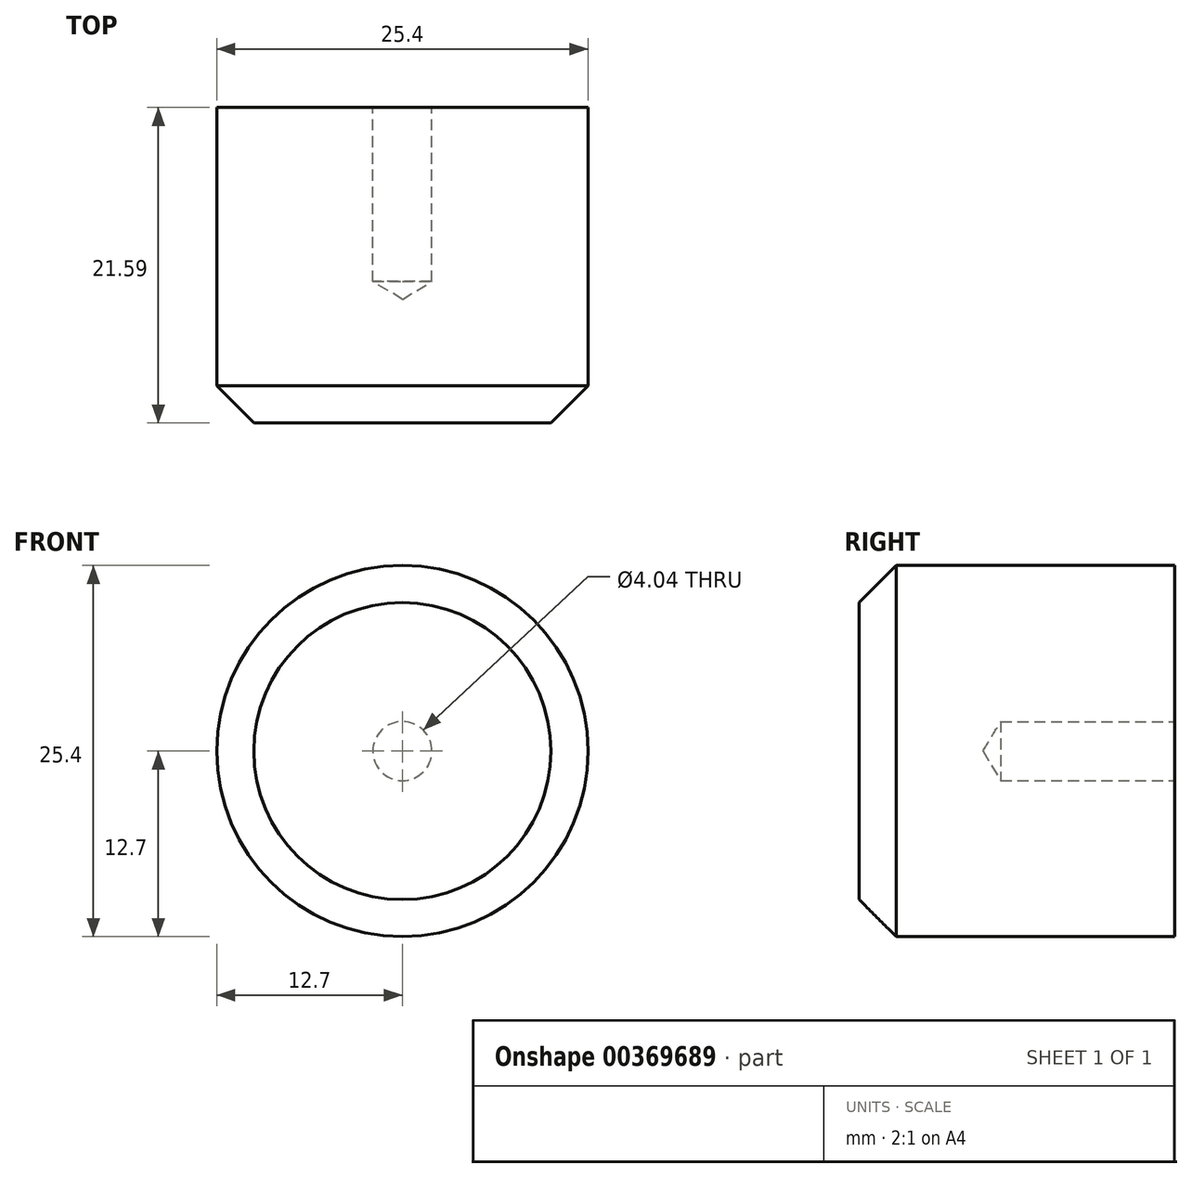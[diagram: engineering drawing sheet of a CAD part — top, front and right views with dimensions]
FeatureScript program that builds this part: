
annotation { "Feature Type Name" : "Feature", "Feature Type Description" : "" }
export const myFeature = defineFeature(function(context is Context, id is Id, definition is map)
    precondition{}
    {
        {
            var Q0;
            Q0=qCreatedBy(makeId("Front.planeOp"),FACE);
            var sketch = newSketch(context, id + "F0", { "sketchPlane" : qUnion([Q0])});
            skCircle(sketch, "E0", {"center": v(0, 0) * mm, "radius": 12.7 * mm});
            skSolve(sketch);
        }
        {
            var Q0;
            Q0 = qSketchRegion(id + "F0", true);
            extrude(context, id + "F1", {"entities" : qUnion([Q0]), "depth" : 21.59 * mm, "offsetDistance" : 25.4 * mm});
        }
        {
            var Q0;
            Q0=makeQuery(id+"F1.opExtrude","CAP_EDGE",EDGE,{"disambiguationData":[OSD([sQuery(id+"F0.wireOp",EDGE,"E0")])],"isStart":false});
            chamfer(context, id + "F2", {"entities" : qUnion([Q0]), "width" : 2.54 * mm, "tangentPropagation" : true});
        }
        {
            var Q0;
            Q0=makeQuery(id+"F1.opExtrude","CAP_FACE",FACE,{"disambiguationData":[OSD([sQuery(id+"F0.wireOp",EDGE,"E0")])],"isStart":true});
            var sketch = newSketch(context, id + "F3", { "sketchPlane" : qUnion([Q0])});
            skPoint(sketch, "E1", {"position": v(0, 0) * mm});
            skSolve(sketch);
        }
        {
            var Q0;
            Q0=sQuery(id+"F3.wireOp",VERTEX,"E1");
            var Q1;
            Q1=makeQuery(id+"F1.opExtrude","SWEPT_BODY",BODY,{"disambiguationData":[OSD([sQuery(id+"F0.wireOp",EDGE,"E0")])]});
            hole(context, id + "F4", {"style" : HoleStyle.SIMPLE, "endStyle" : HoleEndStyle.BLIND, "standardTappedOrClearance" : lookupTablePath({ "standard" : "ANSI", "engagement" : "75%", "pitch" : "32 tpi", "size" : "#10", "type" : "Tapped" }), "standardBlindInLast" : lookupTablePath({ "standard" : "ANSI", "engagement" : "75%", "pitch" : "32 tpi", "size" : "#10", "type" : "Tapped" }), "holeDiameter" : 4.04 * mm, "majorDiameter" : 4.83 * mm, "showTappedDepth" : true, "holeDepth" : 11.9 * mm, "tappedDepth" : 9.52 * mm, "tapClearance" : 3, "startFromSketch" : true, "locations" : qUnion([Q0]), "scope" : qUnion([Q1])});
        }
    });
